# Revit family: Haworth_BuzziScreenMix
name_source: partatom
category: Furniture
revit_build: Autodesk Revit 2018 (Build: 20170223_1515(x64)
units: mm (PartAtom-declared; Revit-internal decimal feet)

## family parameters
Always vertical = Yes
Cut with Voids When Loaded = No
OmniClass Number = 23.40.70.14.64.21
OmniClass Title = Systems Furniture
Room Calculation Point = No
Shared = No
Work Plane-Based = No

## types (8) — shared parameters
Assembly Code = E2020200
Connector Finish = Haworth _ Paint _ Black BTR-9005
High = Yes
Left Zipper Pull Tab = No
Low = No
Manufacturer = Haworth
Medium = No
Model = HCBZ-SMS
Revision Number = 1
Right Zipper Tooth = No
Size = Verify Final Dim. w/ Haworth
URL = http://www.haworth.com
URL - Product = https://www.haworth.com
Warranty = http://www.haworth.com
Zipper Finish = Haworth _ Paint _ Orange BTR-ZORG
zero-valued in all types: Actual Depth, Actual Height, Actual Width, Connection Height

## per-type parameters (varying)
| type | Description | Left Zipper Tooth | Left with Split | Right Zipper Pull Tab | Right with Split |
| HCBZ-SMS-10 | Haworth BuzziScreen Mix Start Panel | Yes | No | No | No |
| HCBZ-SMS-01 | Haworth BuzziScreen Mix Stop Panel | No | No | Yes | No |
| HCBZ-SMS-11 | Haworth BuzziScreen Mix Middle Panel | Yes | No | Yes | No |
| HCBZ-SMS-20 | Haworth BuzziScreen Mix Start Panel with Split | No | Yes | No | No |
| HCBZ-SMS-02 | Haworth BuzziScreen Mix Stop Panel with Split | No | No | No | Yes |
| HCBZ-SMS-12 | Haworth BuzziScreen Mix Middle Panel with Split on Right | Yes | No | No | Yes |
| HCBZ-SMS-21 | Haworth BuzziScreen Mix Middle Panel with Split on Left | No | Yes | Yes | No |
| HCBZ-SMS-22 | Haworth BuzziScreen Mix Middle Panel with Split on Left and Right | No | Yes | No | Yes |

## geometry (parser evidence)
native form markers: Sweep x5
no freeform markers — native parametric forms only
